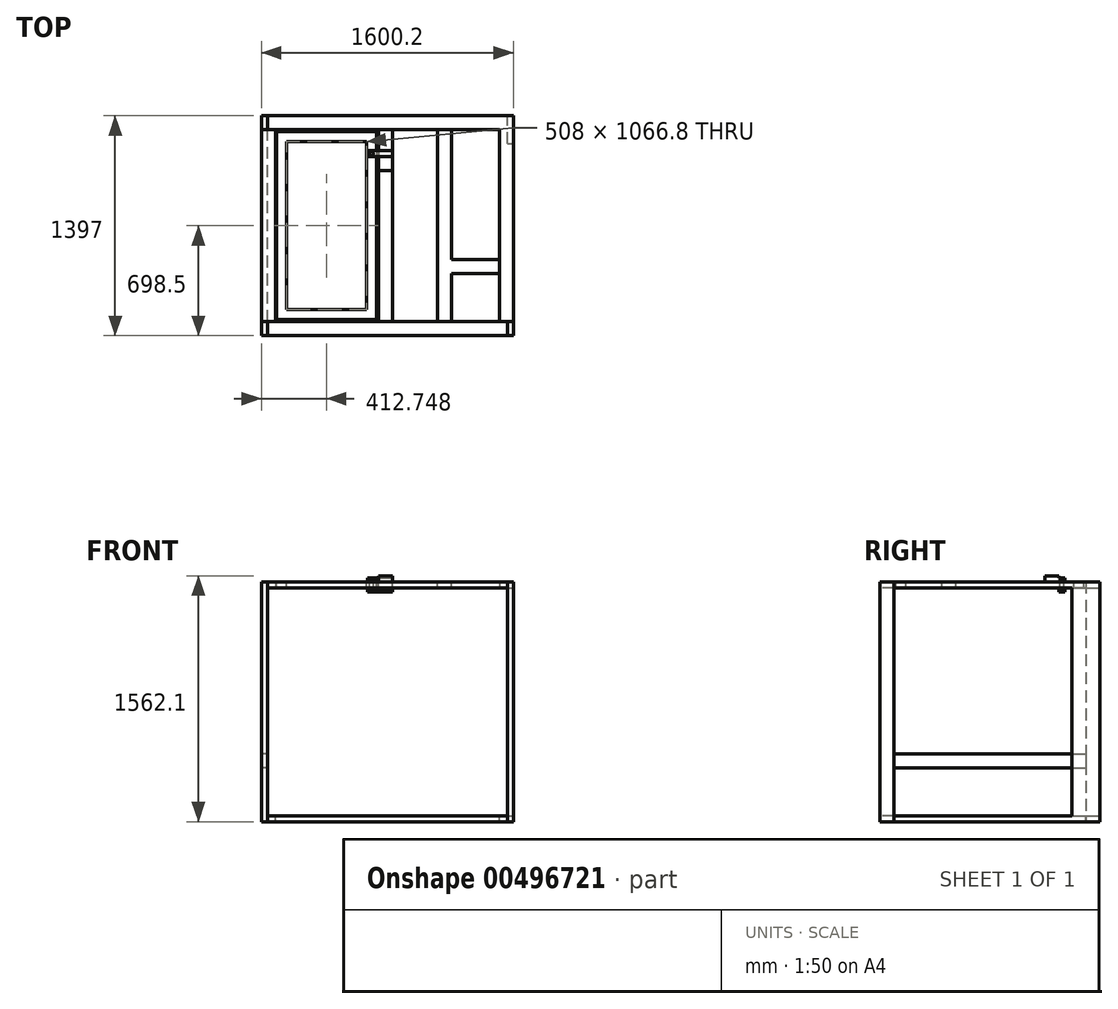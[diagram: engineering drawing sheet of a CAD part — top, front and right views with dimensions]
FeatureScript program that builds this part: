
annotation { "Feature Type Name" : "Feature", "Feature Type Description" : "" }
export const myFeature = defineFeature(function(context is Context, id is Id, definition is map)
    precondition{}
    {
        {
            var Q0;
            Q0=qCreatedBy(makeId("Top.planeOp"),FACE);
            var sketch = newSketch(context, id + "F0", { "sketchPlane" : qUnion([Q0])});
            skLineSegment(sketch, "E0.bottom", {"start": v(-101.05, 0) * mm, "end": v(1422.95, 0) * mm});
            skLineSegment(sketch, "E0.top", {"start": v(-101.05, 88.9) * mm, "end": v(1422.95, 88.9) * mm});
            skLineSegment(sketch, "E0.left", {"start": v(-101.05, 0) * mm, "end": v(-101.05, 88.9) * mm});
            skLineSegment(sketch, "E0.right", {"start": v(1422.95, 0) * mm, "end": v(1422.95, 88.9) * mm});
            skSolve(sketch);
        }
        {
            var Q0;
            Q0=makeQuery(id+"F0.imprint","IMPRINT",FACE,{"disambiguationData":[TD([[makeQuery(id+"F0.imprint","IMPRINT",EDGE,{"derivedFrom":sQuery(id+"F0.wireOp",EDGE,"E0.bottom")}),1.0]])]});
            extrude(context, id + "F1", {"entities" : qUnion([Q0]), "depth" : 38.1 * mm});
        }
        {
            var Q0;
            Q0=makeQuery(id+"F1.opExtrude","SWEPT_FACE",FACE,{"disambiguationData":[OSD([sQuery(id+"F0.wireOp",EDGE,"E0.right")])]});
            var sketch = newSketch(context, id + "F2", { "sketchPlane" : qUnion([Q0])});
            skPoint(sketch, "E1.oppositeSnap0", {"position": v(0, 19.05) * mm});
            skLineSegment(sketch, "E1.bottom", {"start": v(88.9, 38.1) * mm, "end": v(0, 38.1) * mm});
            skLineSegment(sketch, "E1.top", {"start": v(88.9, -1485.9) * mm, "end": v(0, -1485.9) * mm});
            skLineSegment(sketch, "E1.left", {"start": v(88.9, 38.1) * mm, "end": v(88.9, -1485.9) * mm});
            skLineSegment(sketch, "E1.right", {"start": v(0, 38.1) * mm, "end": v(0, -1485.9) * mm});
            skSolve(sketch);
        }
        {
            var Q0;
            {var subQ0=sQuery(id+"F2.wireOp",EDGE,"E1.top");Q0=makeQuery(id+"F2.imprint","IMPRINT",FACE,{"disambiguationData":[TD([[makeQuery(id+"F2.imprint","IMPRINT",EDGE,{"derivedFrom":subQ0}),-1.0]])]});}
            var Q1;
            {var subQ0=sQuery(id+"F2.wireOp",EDGE,"E1.bottom");Q1=makeQuery(id+"F2.imprint","IMPRINT",FACE,{"disambiguationData":[TD([[makeQuery(id+"F2.imprint","IMPRINT",EDGE,{"derivedFrom":subQ0}),-1.0]])]});}
            extrude(context, id + "F3", {"entities" : qUnion([Q0, Q1]), "depth" : 38.1 * mm});
        }
        {
            var Q0;
            Q0=makeQuery(id+"F1.opExtrude","SWEPT_FACE",FACE,{"disambiguationData":[OSD([sQuery(id+"F0.wireOp",EDGE,"E0.left")])]});
            var sketch = newSketch(context, id + "F4", { "sketchPlane" : qUnion([Q0])});
            skPoint(sketch, "E2.oppositeSnap0", {"position": v(-88.9, 19.05) * mm});
            skLineSegment(sketch, "E2.bottom", {"start": v(0, 38.1) * mm, "end": v(-88.9, 38.1) * mm});
            skLineSegment(sketch, "E2.top", {"start": v(0, -1485.9) * mm, "end": v(-88.9, -1485.9) * mm});
            skLineSegment(sketch, "E2.left", {"start": v(0, 38.1) * mm, "end": v(0, -1485.9) * mm});
            skLineSegment(sketch, "E2.right", {"start": v(-88.9, 38.1) * mm, "end": v(-88.9, -1485.9) * mm});
            skSolve(sketch);
        }
        {
            var Q0;
            {var subQ0=sQuery(id+"F4.wireOp",EDGE,"E2.top");Q0=makeQuery(id+"F4.imprint","IMPRINT",FACE,{"disambiguationData":[TD([[makeQuery(id+"F4.imprint","IMPRINT",EDGE,{"derivedFrom":subQ0}),-1.0]])]});}
            var Q1;
            {var subQ0=sQuery(id+"F4.wireOp",EDGE,"E2.bottom");Q1=makeQuery(id+"F4.imprint","IMPRINT",FACE,{"disambiguationData":[TD([[makeQuery(id+"F4.imprint","IMPRINT",EDGE,{"derivedFrom":subQ0}),1.0]])]});}
            extrude(context, id + "F5", {"entities" : qUnion([Q0, Q1]), "depth" : 38.1 * mm});
        }
        {
            var Q0;
            Q0=makeQuery(id+"F5.opExtrude","CAP_FACE",FACE,{"disambiguationData":[OSD([sQuery(id+"F4.wireOp",EDGE,"E2.bottom"),sQuery(id+"F4.wireOp",EDGE,"E2.top"),sQuery(id+"F4.wireOp",EDGE,"E2.left"),sQuery(id+"F4.wireOp",EDGE,"E2.right")])],"isStart":true});
            var sketch = newSketch(context, id + "F6", { "sketchPlane" : qUnion([Q0])});
            skLineSegment(sketch, "E3.bottom", {"start": v(0, -1485.9) * mm, "end": v(88.9, -1485.9) * mm});
            skLineSegment(sketch, "E3.top", {"start": v(0, -1447.8) * mm, "end": v(88.9, -1447.8) * mm});
            skLineSegment(sketch, "E3.left", {"start": v(0, -1485.9) * mm, "end": v(0, -1447.8) * mm});
            skLineSegment(sketch, "E3.right", {"start": v(88.9, -1485.9) * mm, "end": v(88.9, -1447.8) * mm});
            skSolve(sketch);
        }
        {
            var Q0;
            Q0=makeQuery(id+"F6.imprint","IMPRINT",FACE,{"disambiguationData":[TD([[makeQuery(id+"F6.imprint","IMPRINT",EDGE,{"derivedFrom":sQuery(id+"F6.wireOp",EDGE,"E3.bottom")}),1.0]])]});
            extrude(context, id + "F7", {"entities" : qUnion([Q0]), "depth" : 1524 * mm});
        }
        {
            var Q0;
            Q0=makeQuery(id+"F7.opExtrude","SWEPT_FACE",FACE,{"disambiguationData":[OSD([sQuery(id+"F6.wireOp",EDGE,"E3.left")])]});
            var sketch = newSketch(context, id + "F8", { "sketchPlane" : qUnion([Q0])});
            skLineSegment(sketch, "E4.bottom", {"start": v(-139.15, -1485.9) * mm, "end": v(-50.25, -1485.9) * mm});
            skLineSegment(sketch, "E4.top", {"start": v(-139.15, -1447.8) * mm, "end": v(-50.25, -1447.8) * mm});
            skLineSegment(sketch, "E4.left", {"start": v(-139.15, -1485.9) * mm, "end": v(-139.15, -1447.8) * mm});
            skLineSegment(sketch, "E4.right", {"start": v(-50.25, -1485.9) * mm, "end": v(-50.25, -1447.8) * mm});
            skLineSegment(sketch, "E5.bottom", {"start": v(1461.05, -1485.9) * mm, "end": v(1372.15, -1485.9) * mm});
            skLineSegment(sketch, "E5.top", {"start": v(1461.05, -1447.8) * mm, "end": v(1372.15, -1447.8) * mm});
            skLineSegment(sketch, "E5.left", {"start": v(1461.05, -1485.9) * mm, "end": v(1461.05, -1447.8) * mm});
            skLineSegment(sketch, "E5.right", {"start": v(1372.15, -1485.9) * mm, "end": v(1372.15, -1447.8) * mm});
            skLineSegment(sketch, "E6.bottom", {"start": v(1461.05, 38.1) * mm, "end": v(1372.15, 38.1) * mm});
            skLineSegment(sketch, "E6.top", {"start": v(1461.05, 0) * mm, "end": v(1372.15, 0) * mm});
            skLineSegment(sketch, "E6.left", {"start": v(1461.05, 38.1) * mm, "end": v(1461.05, 0) * mm});
            skLineSegment(sketch, "E6.right", {"start": v(1372.15, 38.1) * mm, "end": v(1372.15, 0) * mm});
            skLineSegment(sketch, "E7.bottom", {"start": v(-139.15, 38.1) * mm, "end": v(-50.25, 38.1) * mm});
            skLineSegment(sketch, "E7.top", {"start": v(-139.15, 0) * mm, "end": v(-50.25, 0) * mm});
            skLineSegment(sketch, "E7.left", {"start": v(-139.15, 38.1) * mm, "end": v(-139.15, 0) * mm});
            skLineSegment(sketch, "E7.right", {"start": v(-50.25, 38.1) * mm, "end": v(-50.25, 0) * mm});
            skSolve(sketch);
        }
        {
            var Q0;
            Q0=makeQuery(id+"F8.imprint","IMPRINT",FACE,{"disambiguationData":[TD([[makeQuery(id+"F8.imprint","IMPRINT",EDGE,{"derivedFrom":sQuery(id+"F8.wireOp",EDGE,"E7.bottom")}),-1.0]])]});
            var Q1;
            Q1=makeQuery(id+"F8.imprint","IMPRINT",FACE,{"disambiguationData":[TD([[makeQuery(id+"F8.imprint","IMPRINT",EDGE,{"derivedFrom":sQuery(id+"F8.wireOp",EDGE,"E6.bottom")}),1.0]])]});
            var Q2;
            {var subQ3=sQuery(id+"F8.wireOp",EDGE,"E5.right");Q2=makeQuery(id+"F8.imprint","IMPRINT",FACE,{"disambiguationData":[TD([[makeQuery(id+"F8.imprint","IMPRINT",EDGE,{"derivedFrom":subQ3}),-1.0]])]});}
            var Q3;
            {var subQ2=sQuery(id+"F8.wireOp",EDGE,"E5.left");Q3=makeQuery(id+"F8.imprint","IMPRINT",FACE,{"disambiguationData":[TD([[makeQuery(id+"F8.imprint","IMPRINT",EDGE,{"derivedFrom":subQ2}),1.0]])]});}
            var Q4;
            {var subQ2=sQuery(id+"F8.wireOp",EDGE,"E4.left");Q4=makeQuery(id+"F8.imprint","IMPRINT",FACE,{"disambiguationData":[TD([[makeQuery(id+"F8.imprint","IMPRINT",EDGE,{"derivedFrom":subQ2}),-1.0]])]});}
            var Q5;
            {var subQ3=sQuery(id+"F8.wireOp",EDGE,"E4.right");Q5=makeQuery(id+"F8.imprint","IMPRINT",FACE,{"disambiguationData":[TD([[makeQuery(id+"F8.imprint","IMPRINT",EDGE,{"derivedFrom":subQ3}),1.0]])]});}
            extrude(context, id + "F9", {"entities" : qUnion([Q0, Q1, Q2, Q3, Q4, Q5]), "depth" : 1219.2 * mm});
        }
        {
            var Q0;
            Q0=makeQuery(id+"F9.opExtrude","CAP_FACE",FACE,{"disambiguationData":[OSD([sQuery(id+"F8.wireOp",EDGE,"E5.bottom"),sQuery(id+"F8.wireOp",EDGE,"E5.top"),sQuery(id+"F8.wireOp",EDGE,"E5.left"),sQuery(id+"F8.wireOp",EDGE,"E5.right")])],"isStart":false});
            cPlane(context, id + "F10", {"entities" : qUnion([Q0]), "cplaneType" : CPlaneType.OFFSET, "offset" : 609.6 * mm, "oppositeDirection" : true, "width" : 152.4 * mm, "height" : 152.4 * mm});
        }
        {
            var Q0;
            Q0=makeQuery(id+"F7.opExtrude","SWEPT_BODY",BODY,{"disambiguationData":[OSD([sQuery(id+"F6.wireOp",EDGE,"E3.bottom"),sQuery(id+"F6.wireOp",EDGE,"E3.top"),sQuery(id+"F6.wireOp",EDGE,"E3.left"),sQuery(id+"F6.wireOp",EDGE,"E3.right")])]});
            var Q1;
            Q1=makeQuery(id+"F5.opExtrude","SWEPT_BODY",BODY,{"disambiguationData":[OSD([sQuery(id+"F4.wireOp",EDGE,"E2.bottom"),sQuery(id+"F4.wireOp",EDGE,"E2.top"),sQuery(id+"F4.wireOp",EDGE,"E2.left"),sQuery(id+"F4.wireOp",EDGE,"E2.right")])]});
            var Q2;
            Q2=makeQuery(id+"F1.opExtrude","SWEPT_BODY",BODY,{"disambiguationData":[OSD([sQuery(id+"F0.wireOp",EDGE,"E0.bottom"),sQuery(id+"F0.wireOp",EDGE,"E0.top"),sQuery(id+"F0.wireOp",EDGE,"E0.left"),sQuery(id+"F0.wireOp",EDGE,"E0.right")])]});
            var Q3;
            Q3=makeQuery(id+"F3.opExtrude","SWEPT_BODY",BODY,{"disambiguationData":[OSD([sQuery(id+"F2.wireOp",EDGE,"E1.bottom"),sQuery(id+"F2.wireOp",EDGE,"E1.top"),sQuery(id+"F2.wireOp",EDGE,"E1.left"),sQuery(id+"F2.wireOp",EDGE,"E1.right")])]});
            var Q4;
            Q4=qCreatedBy(id+"F10.planeOp",FACE);
            mirror(context, id + "F11", {"entities" : qUnion([Q0, Q1, Q2, Q3]), "mirrorPlane" : qUnion([Q4])});
        }
        {
            var Q0;
            Q0=makeQuery(id+"F3.opExtrude","SWEPT_FACE",FACE,{"disambiguationData":[OSD([sQuery(id+"F2.wireOp",EDGE,"E1.right")])]});
            extrude(context, id + "F12", {"entities" : qUnion([Q0]), "operationType" : NewBodyOperationType.ADD, "depth" : 88.9 * mm});
        }
        {
            var Q0;
            Q0=makeQuery(id+"F12.boolean.opBoolean","MERGE",FACE,{"derivedFrom":[makeQuery(id+"F1.opExtrude","CAP_FACE",FACE,{"disambiguationData":[OSD([sQuery(id+"F0.wireOp",EDGE,"E0.bottom"),sQuery(id+"F0.wireOp",EDGE,"E0.top"),sQuery(id+"F0.wireOp",EDGE,"E0.left"),sQuery(id+"F0.wireOp",EDGE,"E0.right")])],"isStart":false}),makeQuery(id+"F3.opExtrude","SWEPT_FACE",FACE,{"disambiguationData":[OSD([sQuery(id+"F2.wireOp",EDGE,"E1.bottom")])]}),makeQuery(id+"F9.opExtrude","SWEPT_FACE",FACE,{"disambiguationData":[OSD([sQuery(id+"F8.wireOp",EDGE,"E6.bottom")])]})]});
            var sketch = newSketch(context, id + "F13", { "sketchPlane" : qUnion([Q0])});
            skLineSegment(sketch, "E8.bottom", {"start": v(-43.9, -12.7) * mm, "end": v(591.1, -12.7) * mm});
            skLineSegment(sketch, "E8.top", {"start": v(-43.9, -1206.5) * mm, "end": v(591.1, -1206.5) * mm});
            skLineSegment(sketch, "E8.left", {"start": v(-43.9, -12.7) * mm, "end": v(-43.9, -1206.5) * mm});
            skLineSegment(sketch, "E8.right", {"start": v(591.1, -12.7) * mm, "end": v(591.1, -1206.5) * mm});
            skLineSegment(sketch, "E9.bottom", {"start": v(19.6, -76.2) * mm, "end": v(527.6, -76.2) * mm});
            skLineSegment(sketch, "E9.top", {"start": v(19.6, -1143) * mm, "end": v(527.6, -1143) * mm});
            skLineSegment(sketch, "E9.left", {"start": v(19.6, -76.2) * mm, "end": v(19.6, -1143) * mm});
            skLineSegment(sketch, "E9.right", {"start": v(527.6, -76.2) * mm, "end": v(527.6, -1143) * mm});
            skLineSegment(sketch, "E10", {"start": v(19.6, -1143) * mm, "end": v(19.6, -1206.5) * mm});
            skLineSegment(sketch, "E11", {"start": v(527.6, -1143) * mm, "end": v(527.6, -1206.5) * mm});
            skLineSegment(sketch, "E12", {"start": v(527.6, -12.7) * mm, "end": v(527.6, -76.2) * mm});
            skLineSegment(sketch, "E13", {"start": v(19.6, -76.2) * mm, "end": v(19.6, -12.7) * mm});
            skSolve(sketch);
        }
        {
            var Q0;
            {var subQ0=sQuery(id+"F13.wireOp",EDGE,"E8.left");Q0=makeQuery(id+"F13.imprint","IMPRINT",FACE,{"disambiguationData":[TD([[makeQuery(id+"F13.imprint","IMPRINT",EDGE,{"derivedFrom":subQ0}),1.0]])]});}
            var Q1;
            Q1=makeQuery(id+"F13.imprint","IMPRINT",FACE,{"disambiguationData":[TD([[makeQuery(id+"F13.imprint","IMPRINT",EDGE,{"derivedFrom":sQuery(id+"F13.wireOp",EDGE,"E9.bottom")}),1.0]])]});
            var Q2;
            {var subQ0=sQuery(id+"F13.wireOp",EDGE,"E8.right");Q2=makeQuery(id+"F13.imprint","IMPRINT",FACE,{"disambiguationData":[TD([[makeQuery(id+"F13.imprint","IMPRINT",EDGE,{"derivedFrom":subQ0}),-1.0]])]});}
            var Q3;
            Q3=makeQuery(id+"F13.imprint","IMPRINT",FACE,{"disambiguationData":[TD([[makeQuery(id+"F13.imprint","IMPRINT",EDGE,{"derivedFrom":sQuery(id+"F13.wireOp",EDGE,"E9.top")}),-1.0]])]});
            extrude(context, id + "F14", {"entities" : qUnion([Q0, Q1, Q2, Q3]), "oppositeDirection" : true, "depth" : 38.1 * mm});
        }
        {
            var Q0;
            Q0=makeQuery(id+"F12.boolean.opBoolean","MERGE",FACE,{"derivedFrom":[makeQuery(id+"F1.opExtrude","CAP_FACE",FACE,{"disambiguationData":[OSD([sQuery(id+"F0.wireOp",EDGE,"E0.bottom"),sQuery(id+"F0.wireOp",EDGE,"E0.top"),sQuery(id+"F0.wireOp",EDGE,"E0.left"),sQuery(id+"F0.wireOp",EDGE,"E0.right")])],"isStart":false}),makeQuery(id+"F3.opExtrude","SWEPT_FACE",FACE,{"disambiguationData":[OSD([sQuery(id+"F2.wireOp",EDGE,"E1.bottom")])]}),makeQuery(id+"F9.opExtrude","SWEPT_FACE",FACE,{"disambiguationData":[OSD([sQuery(id+"F8.wireOp",EDGE,"E6.bottom")])]})]});
            var sketch = newSketch(context, id + "F15", { "sketchPlane" : qUnion([Q0])});
            skLineSegment(sketch, "E14.bottom", {"start": v(603.8, 0) * mm, "end": v(692.7, 0) * mm});
            skLineSegment(sketch, "E14.top", {"start": v(603.8, -1219.2) * mm, "end": v(692.7, -1219.2) * mm});
            skLineSegment(sketch, "E14.left", {"start": v(603.8, 0) * mm, "end": v(603.8, -1219.2) * mm});
            skLineSegment(sketch, "E14.right", {"start": v(692.7, 0) * mm, "end": v(692.7, -1219.2) * mm});
            skSolve(sketch);
        }
        {
            var Q0;
            Q0=makeQuery(id+"F15.imprint","IMPRINT",FACE,{"disambiguationData":[TD([[makeQuery(id+"F15.imprint","IMPRINT",EDGE,{"derivedFrom":sQuery(id+"F15.wireOp",EDGE,"E14.bottom")}),-1.0]])]});
            extrude(context, id + "F16", {"entities" : qUnion([Q0]), "oppositeDirection" : true, "depth" : 38.1 * mm});
        }
        {
            var Q0;
            Q0=makeQuery(id+"F14.opExtrude","CAP_FACE",FACE,{"disambiguationData":[OSD([sQuery(id+"F13.wireOp",EDGE,"E8.bottom"),sQuery(id+"F13.wireOp",EDGE,"E8.top"),sQuery(id+"F13.wireOp",EDGE,"E8.left"),sQuery(id+"F13.wireOp",EDGE,"E8.right"),sQuery(id+"F13.wireOp",EDGE,"E9.bottom"),sQuery(id+"F13.wireOp",EDGE,"E9.top"),sQuery(id+"F13.wireOp",EDGE,"E9.left"),sQuery(id+"F13.wireOp",EDGE,"E9.right")])],"isStart":true});
            var sketch = newSketch(context, id + "F17", { "sketchPlane" : qUnion([Q0])});
            skCircle(sketch, "E15", {"center": v(559.35, -152.4) * mm, "radius": 12.7 * mm});
            skSolve(sketch);
        }
        {
            var Q0;
            Q0=makeQuery(id+"F17.imprint","IMPRINT",FACE,{"disambiguationData":[TD([[makeQuery(id+"F17.imprint","IMPRINT",EDGE,{"derivedFrom":sQuery(id+"F17.wireOp",EDGE,"E15")}),1.0]])]});
            extrude(context, id + "F18", {"entities" : qUnion([Q0]), "depth" : 25.4 * mm, "hasSecondDirection" : true, "secondDirectionOppositeDirection" : true, "secondDirectionDepth" : 63.5 * mm});
        }
        {
            var Q0;
            Q0=makeQuery(id+"F18.opExtrude","CAP_FACE",FACE,{"disambiguationData":[OSD([sQuery(id+"F17.wireOp",EDGE,"E15")])],"isStart":false});
            var sketch = newSketch(context, id + "F19", { "sketchPlane" : qUnion([Q0])});
            skLineSegment(sketch, "E16.bottom", {"start": v(533.95, -171.45) * mm, "end": v(692.7, -171.45) * mm});
            skLineSegment(sketch, "E16.top", {"start": v(533.95, -133.35) * mm, "end": v(692.7, -133.35) * mm});
            skLineSegment(sketch, "E16.left", {"start": v(533.95, -171.45) * mm, "end": v(533.95, -133.35) * mm});
            skLineSegment(sketch, "E16.right", {"start": v(692.7, -171.45) * mm, "end": v(692.7, -133.35) * mm});
            skSolve(sketch);
        }
        {
            var Q0;
            Q0=makeQuery(id+"F19.imprint","IMPRINT",FACE,{"disambiguationData":[TD([[makeQuery(id+"F19.imprint","IMPRINT",EDGE,{"derivedFrom":sQuery(id+"F19.wireOp",EDGE,"E16.bottom")}),1.0]])]});
            extrude(context, id + "F20", {"entities" : qUnion([Q0]), "operationType" : NewBodyOperationType.ADD, "oppositeDirection" : true, "depth" : 19.05 * mm});
        }
        {
            var Q0;
            Q0=makeQuery(id+"F16.opExtrude","CAP_FACE",FACE,{"disambiguationData":[OSD([sQuery(id+"F15.wireOp",EDGE,"E14.bottom"),sQuery(id+"F15.wireOp",EDGE,"E14.top"),sQuery(id+"F15.wireOp",EDGE,"E14.left"),sQuery(id+"F15.wireOp",EDGE,"E14.right")])],"isStart":true});
            cPlane(context, id + "F21", {"entities" : qUnion([Q0]), "cplaneType" : CPlaneType.OFFSET, "offset" : 19.05 * mm, "oppositeDirection" : true, "width" : 152.4 * mm, "height" : 152.4 * mm});
        }
        {
            var Q0;
            Q0=makeQuery(id+"F18.opExtrude","SWEPT_BODY",BODY,{"disambiguationData":[OSD([sQuery(id+"F17.wireOp",EDGE,"E15")])]});
            var Q1;
            Q1=qCreatedBy(id+"F21.planeOp",FACE);
            mirror(context, id + "F22", {"entities" : qUnion([Q0]), "mirrorPlane" : qUnion([Q1])});
        }
        {
            var Q0;
            Q0=makeQuery(id+"F16.opExtrude","CAP_FACE",FACE,{"disambiguationData":[OSD([sQuery(id+"F15.wireOp",EDGE,"E14.bottom"),sQuery(id+"F15.wireOp",EDGE,"E14.top"),sQuery(id+"F15.wireOp",EDGE,"E14.left"),sQuery(id+"F15.wireOp",EDGE,"E14.right")])],"isStart":true});
            var sketch = newSketch(context, id + "F23", { "sketchPlane" : qUnion([Q0])});
            skLineSegment(sketch, "E17.bottom", {"start": v(603.8, -171.45) * mm, "end": v(692.7, -171.45) * mm});
            skLineSegment(sketch, "E17.top", {"start": v(603.8, -260.35) * mm, "end": v(692.7, -260.35) * mm});
            skLineSegment(sketch, "E17.left", {"start": v(603.8, -171.45) * mm, "end": v(603.8, -260.35) * mm});
            skLineSegment(sketch, "E17.right", {"start": v(692.7, -171.45) * mm, "end": v(692.7, -260.35) * mm});
            skSolve(sketch);
        }
        {
            var Q0;
            Q0=makeQuery(id+"F23.imprint","IMPRINT",FACE,{"disambiguationData":[TD([[makeQuery(id+"F23.imprint","IMPRINT",EDGE,{"derivedFrom":sQuery(id+"F23.wireOp",EDGE,"E17.bottom")}),-1.0]])]});
            extrude(context, id + "F24", {"entities" : qUnion([Q0]), "operationType" : NewBodyOperationType.ADD, "depth" : 38.1 * mm});
        }
        {
            var Q0;
            Q0=makeQuery(id+"F12.boolean.opBoolean","MERGE",FACE,{"derivedFrom":[makeQuery(id+"F1.opExtrude","CAP_FACE",FACE,{"disambiguationData":[OSD([sQuery(id+"F0.wireOp",EDGE,"E0.bottom"),sQuery(id+"F0.wireOp",EDGE,"E0.top"),sQuery(id+"F0.wireOp",EDGE,"E0.left"),sQuery(id+"F0.wireOp",EDGE,"E0.right")])],"isStart":false}),makeQuery(id+"F3.opExtrude","SWEPT_FACE",FACE,{"disambiguationData":[OSD([sQuery(id+"F2.wireOp",EDGE,"E1.bottom")])]}),makeQuery(id+"F9.opExtrude","SWEPT_FACE",FACE,{"disambiguationData":[OSD([sQuery(id+"F8.wireOp",EDGE,"E6.bottom")])]})]});
            var sketch = newSketch(context, id + "F25", { "sketchPlane" : qUnion([Q0])});
            skLineSegment(sketch, "E18.bottom", {"start": v(1067.35, 0) * mm, "end": v(978.45, 0) * mm});
            skLineSegment(sketch, "E18.top", {"start": v(1067.35, -1219.2) * mm, "end": v(978.45, -1219.2) * mm});
            skLineSegment(sketch, "E18.left", {"start": v(1067.35, 0) * mm, "end": v(1067.35, -1219.2) * mm});
            skLineSegment(sketch, "E18.right", {"start": v(978.45, 0) * mm, "end": v(978.45, -1219.2) * mm});
            skLineSegment(sketch, "E19.bottom", {"start": v(1067.35, -914.4) * mm, "end": v(1372.15, -914.4) * mm});
            skLineSegment(sketch, "E19.top", {"start": v(1067.35, -825.5) * mm, "end": v(1372.15, -825.5) * mm});
            skLineSegment(sketch, "E19.left", {"start": v(1067.35, -914.4) * mm, "end": v(1067.35, -825.5) * mm});
            skLineSegment(sketch, "E19.right", {"start": v(1372.15, -914.4) * mm, "end": v(1372.15, -825.5) * mm});
            skSolve(sketch);
        }
        {
            var Q0;
            Q0=makeQuery(id+"F25.imprint","IMPRINT",FACE,{"disambiguationData":[TD([[makeQuery(id+"F25.imprint","IMPRINT",EDGE,{"derivedFrom":sQuery(id+"F25.wireOp",EDGE,"E19.bottom")}),1.0]])]});
            var Q1;
            {var subQ3=sQuery(id+"F25.wireOp",EDGE,"E18.bottom");Q1=makeQuery(id+"F25.imprint","IMPRINT",FACE,{"disambiguationData":[TD([[makeQuery(id+"F25.imprint","IMPRINT",EDGE,{"derivedFrom":subQ3}),-1.0]])]});}
            extrude(context, id + "F26", {"entities" : qUnion([Q0, Q1]), "oppositeDirection" : true, "depth" : 38.1 * mm});
        }
        {
            var Q0;
            Q0=makeQuery(id+"F5.opExtrude","CAP_FACE",FACE,{"disambiguationData":[OSD([sQuery(id+"F4.wireOp",EDGE,"E2.bottom"),sQuery(id+"F4.wireOp",EDGE,"E2.top"),sQuery(id+"F4.wireOp",EDGE,"E2.left"),sQuery(id+"F4.wireOp",EDGE,"E2.right")])],"isStart":false});
            var sketch = newSketch(context, id + "F27", { "sketchPlane" : qUnion([Q0])});
            skLineSegment(sketch, "E20.bottom", {"start": v(1219.2, -1054.1) * mm, "end": v(0, -1054.1) * mm});
            skLineSegment(sketch, "E20.top", {"start": v(1219.2, -1143) * mm, "end": v(0, -1143) * mm});
            skLineSegment(sketch, "E20.left", {"start": v(1219.2, -1054.1) * mm, "end": v(1219.2, -1143) * mm});
            skLineSegment(sketch, "E20.right", {"start": v(0, -1054.1) * mm, "end": v(0, -1143) * mm});
            skLineSegment(sketch, "E21.bottom", {"start": v(914.4, -1143) * mm, "end": v(825.5, -1143) * mm});
            skLineSegment(sketch, "E21.top", {"start": v(914.4, -1447.8) * mm, "end": v(825.5, -1447.8) * mm});
            skLineSegment(sketch, "E21.left", {"start": v(914.4, -1143) * mm, "end": v(914.4, -1447.8) * mm});
            skLineSegment(sketch, "E21.right", {"start": v(825.5, -1143) * mm, "end": v(825.5, -1447.8) * mm});
            skSolve(sketch);
        }
        {
            var Q0;
            Q0=makeQuery(id+"F27.imprint","IMPRINT",FACE,{"disambiguationData":[TD([[makeQuery(id+"F27.imprint","IMPRINT",EDGE,{"derivedFrom":sQuery(id+"F27.wireOp",EDGE,"E20.bottom")}),1.0]])]});
            var Q1;
            Q1=makeQuery(id+"F27.imprint","IMPRINT",FACE,{"disambiguationData":[TD([[makeQuery(id+"F27.imprint","IMPRINT",EDGE,{"derivedFrom":sQuery(id+"F27.wireOp",EDGE,"E21.bottom")}),1.0]])]});
            extrude(context, id + "F28", {"entities" : qUnion([Q0, Q1]), "oppositeDirection" : true, "depth" : 38.1 * mm});
        }
    });
